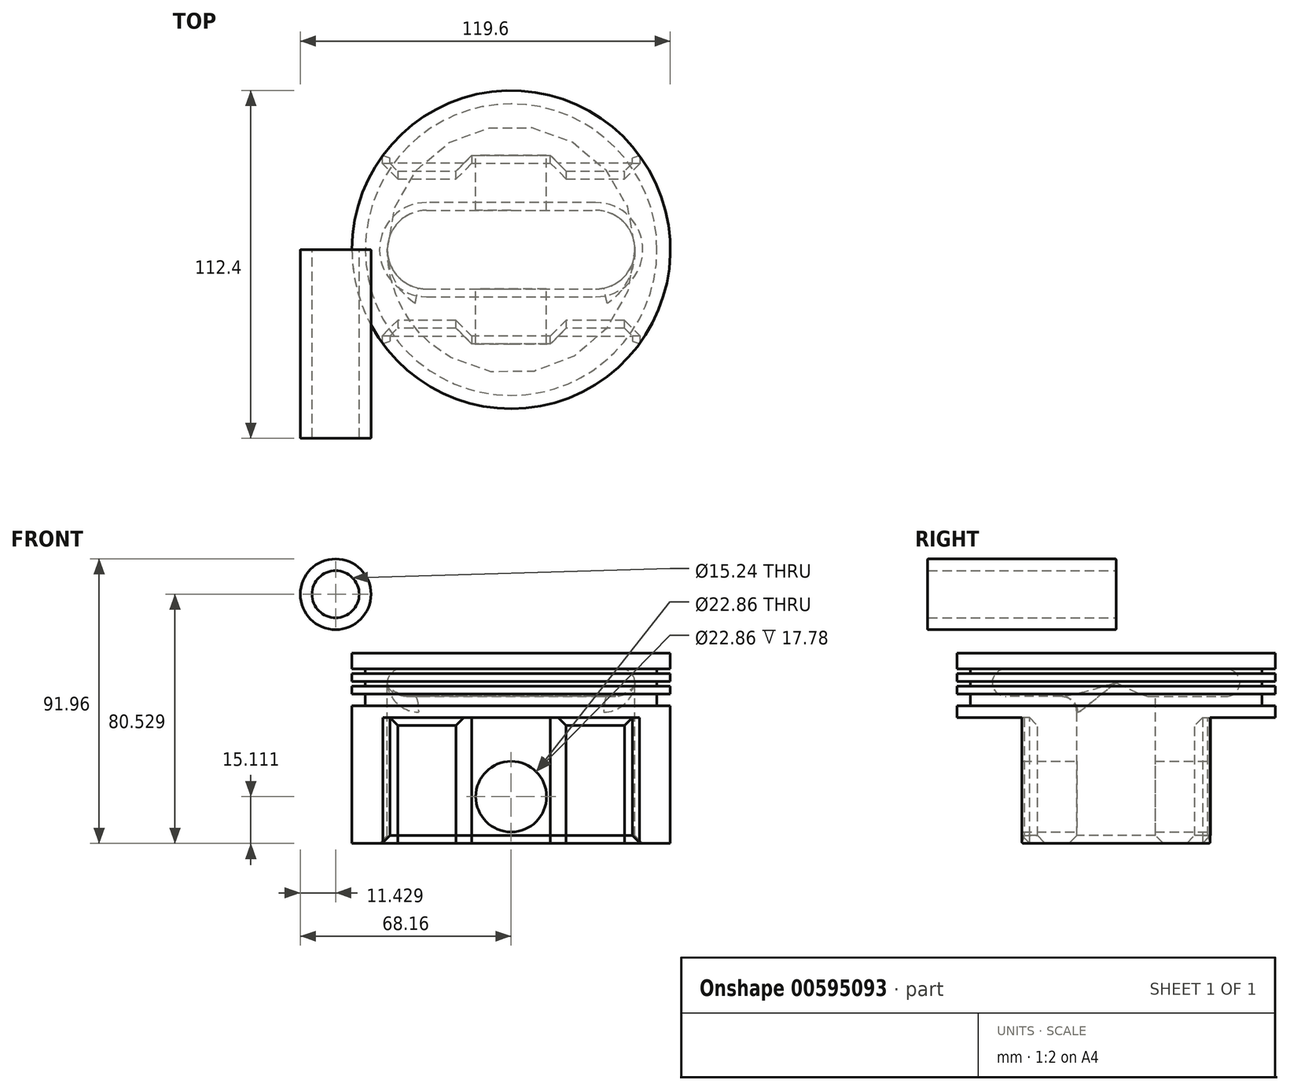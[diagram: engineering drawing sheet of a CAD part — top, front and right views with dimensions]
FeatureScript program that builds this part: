
annotation { "Feature Type Name" : "Feature", "Feature Type Description" : "" }
export const myFeature = defineFeature(function(context is Context, id is Id, definition is map)
    precondition{}
    {
        {
            var Q0;
            Q0=qCreatedBy(makeId("Front.planeOp"),FACE);
            var sketch = newSketch(context, id + "F0", { "sketchPlane" : qUnion([Q0])});
            skLineSegment(sketch, "E0", {"start": v(0, 41.43) * mm, "end": v(-51.44, 41.43) * mm});
            skLineSegment(sketch, "E1", {"start": v(-51.43, 41.43) * mm, "end": v(-51.43, 36.35) * mm});
            skLineSegment(sketch, "E2", {"start": v(-51.44, 36.35) * mm, "end": v(-47.12, 36.35) * mm});
            skLineSegment(sketch, "E3", {"start": v(-47.12, 36.35) * mm, "end": v(-47.12, 34.82) * mm});
            skLineSegment(sketch, "E4", {"start": v(-47.12, 34.82) * mm, "end": v(-51.44, 34.82) * mm});
            skLineSegment(sketch, "E5", {"start": v(-51.43, 34.82) * mm, "end": v(-51.43, 32.28) * mm});
            skLineSegment(sketch, "E6", {"start": v(-51.44, 32.28) * mm, "end": v(-47.12, 32.28) * mm});
            skLineSegment(sketch, "E7", {"start": v(-47.12, 32.28) * mm, "end": v(-47.12, 30.76) * mm});
            skLineSegment(sketch, "E8", {"start": v(-47.12, 30.76) * mm, "end": v(-51.44, 30.76) * mm});
            skLineSegment(sketch, "E9", {"start": v(-51.44, 30.76) * mm, "end": v(-51.44, 28.22) * mm});
            skLineSegment(sketch, "E10", {"start": v(-51.44, 28.22) * mm, "end": v(-47.12, 28.22) * mm});
            skLineSegment(sketch, "E11", {"start": v(-47.12, 28.22) * mm, "end": v(-47.12, 24.4) * mm});
            skLineSegment(sketch, "E12", {"start": v(-47.12, 24.4) * mm, "end": v(-51.44, 24.4) * mm});
            skLineSegment(sketch, "E13", {"start": v(-51.44, 24.4) * mm, "end": v(-51.44, 20.6) * mm});
            skLineSegment(sketch, "E14", {"start": v(-51.44, 20.6) * mm, "end": v(-40, 20.6) * mm});
            skLineSegment(sketch, "E15", {"start": v(0, 20.6) * mm, "end": v(0, 27.46) * mm});
            skLineSegment(sketch, "E16", {"start": v(0, 36.35) * mm, "end": v(-35.56, 36.35) * mm});
            skPoint(sketch, "E17.orphan", {"position": v(-35.56, 27.46) * mm});
            skArc(sketch, "E18", {"start": v(-35.56, 36.35) * mm, "mid": v(-40, 31.9) * mm, "end": v(-35.56, 27.46) * mm});
            skLineSegment(sketch, "E19", {"start": v(-35.56, 27.46) * mm, "end": v(0, 27.46) * mm});
            skLineSegment(sketch, "E20", {"start": v(-40, 20.6) * mm, "end": v(0, 20.6) * mm});
            skLineSegment(sketch, "E21.trimOffspring", {"start": v(0, 36.35) * mm, "end": v(0, 41.43) * mm});
            skSolve(sketch);
        }
        {
            var Q0;
            {var subQ0=sQuery(id+"F0.wireOp",EDGE,"E0");Q0=makeQuery(id+"F0.imprint","IMPRINT",FACE,{"disambiguationData":[TD([[makeQuery(id+"F0.imprint","IMPRINT",EDGE,{"derivedFrom":subQ0}),1.0]])]});}
            var Q1;
            Q1=sQuery(id+"F0.wireOp",EDGE,"E15");
            revolve(context, id + "F1", {"entities" : qUnion([Q0]), "axis" : qUnion([Q1]), "revolveType" : RevolveType.FULL});
        }
        {
            var Q0;
            Q0=makeQuery(id+"F1.opRevolve","SWEPT_FACE",FACE,{"disambiguationData":[OSD([sQuery(id+"F0.wireOp",EDGE,"E14")])]});
            var sketch = newSketch(context, id + "F2", { "sketchPlane" : qUnion([Q0])});
            skLineSegment(sketch, "E22", {"start": v(-39.2, 25.4) * mm, "end": v(-15.24, 25.4) * mm});
            skLineSegment(sketch, "E23", {"start": v(-13.04, 12.7) * mm, "end": v(16, 12.7) * mm, "construction": true});
            skLineSegment(sketch, "E24", {"start": v(-39.2, 25.4) * mm, "end": v(-39.2, 33.3) * mm});
            skLineSegment(sketch, "E25.MirrorCS", {"start": v(39.2, 25.4) * mm, "end": v(39.2, 33.3) * mm});
            skLineSegment(sketch, "E26.MirrorCS", {"start": v(-39.2, -25.4) * mm, "end": v(-15.24, -25.4) * mm});
            skLineSegment(sketch, "E27.MirrorCS", {"start": v(-39.2, -25.4) * mm, "end": v(-39.2, -33.3) * mm});
            skLineSegment(sketch, "E28", {"start": v(0, 12.7) * mm, "end": v(27.3, 12.7) * mm});
            skPoint(sketch, "E28.startSnap0", {"position": v(1.48, 12.7) * mm});
            skLineSegment(sketch, "E29.MirrorCS", {"start": v(0, -12.7) * mm, "end": v(27.3, -12.7) * mm});
            skArc(sketch, "E30", {"start": v(27.3, 12.7) * mm, "mid": v(40, 0) * mm, "end": v(27.3, -12.7) * mm});
            skArc(sketch, "E31.MirrorCS", {"start": v(-27.3, 12.7) * mm, "mid": v(-40, 0) * mm, "end": v(-27.3, -12.7) * mm});
            skLineSegment(sketch, "E32.MirrorCS", {"start": v(0, 12.7) * mm, "end": v(-27.3, 12.7) * mm});
            skLineSegment(sketch, "E33.MirrorCS", {"start": v(0, -12.7) * mm, "end": v(-27.3, -12.7) * mm});
            skLineSegment(sketch, "E34", {"start": v(-15.24, 25.4) * mm, "end": v(-15.24, 30.48) * mm});
            skLineSegment(sketch, "E35", {"start": v(-15.24, 30.48) * mm, "end": v(0, 30.48) * mm});
            skLineSegment(sketch, "E36.MirrorCS", {"start": v(15.24, 30.48) * mm, "end": v(0, 30.48) * mm});
            skLineSegment(sketch, "E37.MirrorCS", {"start": v(15.24, 25.4) * mm, "end": v(15.24, 30.48) * mm});
            skLineSegment(sketch, "E38.MirrorCS", {"start": v(-15.24, -30.48) * mm, "end": v(0, -30.48) * mm});
            skLineSegment(sketch, "E39.MirrorCS", {"start": v(15.24, -30.48) * mm, "end": v(0, -30.48) * mm});
            skLineSegment(sketch, "E40.MirrorCS", {"start": v(15.24, -25.4) * mm, "end": v(15.24, -30.48) * mm});
            skLineSegment(sketch, "E41.MirrorCS", {"start": v(-15.24, -25.4) * mm, "end": v(-15.24, -30.48) * mm});
            skLineSegment(sketch, "E42.trimOffspring", {"start": v(15.24, -25.4) * mm, "end": v(39.2, -25.4) * mm});
            skLineSegment(sketch, "E43.trimOffspring", {"start": v(15.24, 25.4) * mm, "end": v(39.2, 25.4) * mm});
            skPoint(sketch, "E44.orphan", {"position": v(44.73, 25.4) * mm});
            skLineSegment(sketch, "E45.MirrorCS", {"start": v(39.2, -25.4) * mm, "end": v(39.2, -33.3) * mm});
            skPoint(sketch, "E46.orphan", {"position": v(44.73, -25.4) * mm});
            skSolve(sketch);
        }
        {
            var Q0;
            Q0=makeQuery(id+"F2.imprint","IMPRINT",FACE,{"disambiguationData":[TD([[makeQuery(id+"F2.imprint","IMPRINT",EDGE,{"derivedFrom":sQuery(id+"F2.wireOp",EDGE,"E22")}),-1.0]])]});
            extrude(context, id + "F3", {"entities" : qUnion([Q0]), "operationType" : NewBodyOperationType.ADD, "depth" : 40.64 * mm, "offsetDistance" : 25.4 * mm});
        }
        {
            var Q0;
            Q0=makeQuery(id+"F3.opExtrude","SWEPT_FACE",FACE,{"disambiguationData":[OSD([sQuery(id+"F2.wireOp",EDGE,"E38.MirrorCS"),sQuery(id+"F2.wireOp",EDGE,"E39.MirrorCS")])]});
            var sketch = newSketch(context, id + "F4", { "sketchPlane" : qUnion([Q0])});
            skCircle(sketch, "E47", {"center": v(0, -4.93) * mm, "radius": 11.43 * mm});
            skPoint(sketch, "E47.centerSnap0", {"position": v(-15.24, 0.28) * mm});
            skSolve(sketch);
        }
        {
            var Q0;
            Q0=makeQuery(id+"F4.imprint","IMPRINT",FACE,{"disambiguationData":[TD([[makeQuery(id+"F4.imprint","IMPRINT",EDGE,{"derivedFrom":sQuery(id+"F4.wireOp",EDGE,"E47")}),1.0]])]});
            extrude(context, id + "F5", {"entities" : qUnion([Q0]), "operationType" : NewBodyOperationType.REMOVE, "oppositeDirection" : true, "depth" : 77.72 * mm, "offsetDistance" : 25.4 * mm});
        }
        {
            var Q0;
            Q0=makeQuery(id+"F3.opExtrude","SWEPT_EDGE",EDGE,{"disambiguationData":[OSD([sQuery(id+"F2.wireOp",EDGE,"E38.MirrorCS"),sQuery(id+"F2.wireOp",EDGE,"E41.MirrorCS")])]});
            var Q1;
            Q1=makeQuery(id+"F3.opExtrude","SWEPT_EDGE",EDGE,{"disambiguationData":[OSD([sQuery(id+"F2.wireOp",EDGE,"E26.MirrorCS"),sQuery(id+"F2.wireOp",EDGE,"E41.MirrorCS")])]});
            var Q2;
            Q2=makeQuery(id+"F3.opExtrude","CAP_EDGE",EDGE,{"disambiguationData":[OSD([sQuery(id+"F2.wireOp",EDGE,"E26.MirrorCS")])],"isStart":false});
            var Q3;
            Q3=makeQuery(id+"F3.opExtrude","CAP_EDGE",EDGE,{"disambiguationData":[OSD([sQuery(id+"F2.wireOp",EDGE,"E27.MirrorCS")])],"isStart":false});
            var Q4;
            Q4=makeQuery(id+"F3.opExtrude","CAP_EDGE",EDGE,{"disambiguationData":[OSD([sQuery(id+"F2.wireOp",EDGE,"E42.trimOffspring")])],"isStart":false});
            var Q5;
            Q5=makeQuery(id+"F3.opExtrude","SWEPT_FACE",FACE,{"disambiguationData":[OSD([sQuery(id+"F2.wireOp",EDGE,"E26.MirrorCS")])]});
            var Q6;
            Q6=makeQuery(id+"F3.opExtrude","SWEPT_FACE",FACE,{"disambiguationData":[OSD([sQuery(id+"F2.wireOp",EDGE,"E42.trimOffspring")])]});
            var Q7;
            Q7=makeQuery(id+"F3.opExtrude","SWEPT_EDGE",EDGE,{"disambiguationData":[OSD([sQuery(id+"F2.wireOp",EDGE,"E39.MirrorCS"),sQuery(id+"F2.wireOp",EDGE,"E40.MirrorCS")])]});
            var Q8;
            Q8=makeQuery(id+"F3.opExtrude","CAP_EDGE",EDGE,{"disambiguationData":[OSD([sQuery(id+"F2.wireOp",EDGE,"E38.MirrorCS"),sQuery(id+"F2.wireOp",EDGE,"E39.MirrorCS")])],"isStart":false});
            var Q9;
            Q9=makeQuery(id+"F3.opExtrude","SWEPT_FACE",FACE,{"disambiguationData":[OSD([sQuery(id+"F2.wireOp",EDGE,"E43.trimOffspring")])]});
            var Q10;
            Q10=makeQuery(id+"F3.opExtrude","SWEPT_FACE",FACE,{"disambiguationData":[OSD([sQuery(id+"F2.wireOp",EDGE,"E22")])]});
            var Q11;
            Q11=makeQuery(id+"F3.opExtrude","CAP_EDGE",EDGE,{"disambiguationData":[OSD([sQuery(id+"F2.wireOp",EDGE,"E35"),sQuery(id+"F2.wireOp",EDGE,"E36.MirrorCS")])],"isStart":false});
            var Q12;
            Q12=makeQuery(id+"F3.opExtrude","SWEPT_EDGE",EDGE,{"disambiguationData":[OSD([sQuery(id+"F2.wireOp",EDGE,"E36.MirrorCS"),sQuery(id+"F2.wireOp",EDGE,"E37.MirrorCS")])]});
            var Q13;
            Q13=makeQuery(id+"F3.opExtrude","SWEPT_EDGE",EDGE,{"disambiguationData":[OSD([sQuery(id+"F2.wireOp",EDGE,"E34"),sQuery(id+"F2.wireOp",EDGE,"E35")])]});
            chamfer(context, id + "F6", {"entities" : qUnion([Q0, Q1, Q2, Q3, Q4, Q5, Q6, Q7, Q8, Q9, Q10, Q11, Q12, Q13]), "width" : 2.54 * mm, "tangentPropagation" : true});
        }
        {
            var Q0;
            Q0=makeQuery(id+"F3.opExtrude","SWEPT_EDGE",EDGE,{"disambiguationData":[OSD([sQuery(id+"F0.wireOp",EDGE,"E13"),sQuery(id+"F0.wireOp",EDGE,"E14"),sQuery(id+"F2.wireOp",EDGE,"E45.MirrorCS")])]});
            var Q1;
            Q1=makeQuery(id+"F3.opExtrude","SWEPT_EDGE",EDGE,{"disambiguationData":[OSD([sQuery(id+"F0.wireOp",EDGE,"E13"),sQuery(id+"F0.wireOp",EDGE,"E14"),sQuery(id+"F2.wireOp",EDGE,"E27.MirrorCS")])]});
            var Q2;
            Q2=makeQuery(id+"F3.opExtrude","SWEPT_EDGE",EDGE,{"disambiguationData":[OSD([sQuery(id+"F0.wireOp",EDGE,"E13"),sQuery(id+"F0.wireOp",EDGE,"E14"),sQuery(id+"F2.wireOp",EDGE,"E24")])]});
            var Q3;
            Q3=makeQuery(id+"F3.opExtrude","SWEPT_EDGE",EDGE,{"disambiguationData":[OSD([sQuery(id+"F0.wireOp",EDGE,"E13"),sQuery(id+"F0.wireOp",EDGE,"E14"),sQuery(id+"F2.wireOp",EDGE,"E25.MirrorCS")])]});
            chamfer(context, id + "F7", {"entities" : qUnion([Q0, Q1, Q2, Q3]), "width" : 1.27 * mm, "tangentPropagation" : true});
        }
        {
            var Q0;
            Q0=makeQuery(id+"F3.opExtrude","CAP_EDGE",EDGE,{"disambiguationData":[OSD([sQuery(id+"F2.wireOp",EDGE,"E30")])],"isStart":false});
            chamfer(context, id + "F8", {"entities" : qUnion([Q0]), "width" : 2.54 * mm, "tangentPropagation" : true});
        }
        {
            var Q0;
            Q0=makeQuery(id+"F3.boolean.opBoolean","SPLIT",FACE,{"disambiguationData":[TD([makeQuery(id+"F3.opExtrude","SWEPT_FACE",FACE,{"disambiguationData":[OSD([sQuery(id+"F2.wireOp",EDGE,"E30")])]})])],"derivedFrom":makeQuery(id+"F1.opRevolve","SWEPT_FACE",FACE,{"disambiguationData":[OSD([sQuery(id+"F0.wireOp",EDGE,"E14"),sQuery(id+"F0.wireOp",EDGE,"E20")])]})});
            extrude(context, id + "F9", {"entities" : qUnion([Q0]), "operationType" : NewBodyOperationType.REMOVE, "oppositeDirection" : true, "depth" : 11.18 * mm, "offsetDistance" : 25.4 * mm});
        }
        {
            var Q0;
            Q0=makeQuery(id+"F9.boolean.opBoolean","INTERSECT",EDGE,{"derivedFrom":[makeQuery(id+"F1.opRevolve","SWEPT_FACE",FACE,{"disambiguationData":[OSD([sQuery(id+"F0.wireOp",EDGE,"E19")])]}),makeQuery(id+"F9.opExtrude","SWEPT_FACE",FACE,{"disambiguationData":[OSD([sQuery(id+"F2.wireOp",EDGE,"E28"),sQuery(id+"F2.wireOp",EDGE,"E32.MirrorCS")])]})]});
            fillet(context, id + "F10", {"entities" : qUnion([Q0]), "radius" : 5.08 * mm, "tangentPropagation" : true, "allowEdgeOverflow" : false});
        }
        {
            var Q0;
            Q0=qCreatedBy(makeId("Front.planeOp"),FACE);
            var sketch = newSketch(context, id + "F11", { "sketchPlane" : qUnion([Q0])});
            skCircle(sketch, "E48", {"center": v(-56.73, 60.49) * mm, "radius": 11.43 * mm});
            skCircle(sketch, "E49.0", {"center": v(-56.73, 60.49) * mm, "radius": 7.62 * mm});
            skSolve(sketch);
        }
        {
            var Q0;
            Q0=makeQuery(id+"F11.imprint","IMPRINT",FACE,{"disambiguationData":[TD([[makeQuery(id+"F11.imprint","IMPRINT",EDGE,{"derivedFrom":sQuery(id+"F11.wireOp",EDGE,"E48")}),1.0]])]});
            extrude(context, id + "F12", {"entities" : qUnion([Q0]), "depth" : 60.96 * mm, "offsetDistance" : 25.4 * mm});
        }
        {
            var Q0;
            Q0=makeQuery(id+"F12.opExtrude","CAP_FACE",FACE,{"disambiguationData":[OSD([sQuery(id+"F11.wireOp",EDGE,"E48"),sQuery(id+"F11.wireOp",EDGE,"E49.0")])],"isStart":false});
            var Q1;
            Q1=makeQuery(id+"F12.opExtrude","CAP_FACE",FACE,{"disambiguationData":[OSD([sQuery(id+"F11.wireOp",EDGE,"E48"),sQuery(id+"F11.wireOp",EDGE,"E49.0")])],"isStart":true});
            var Q2;
            Q2=makeQuery(id+"F5.boolean.opBoolean","COPY",EDGE,{"derivedFrom":makeQuery(id+"F5.opExtrude","CAP_EDGE",EDGE,{"disambiguationData":[OSD([sQuery(id+"F4.wireOp",EDGE,"E47")])],"isStart":true})});
            var Q3;
            Q3=makeQuery(id+"F5.boolean.opBoolean","INTERSECT",EDGE,{"derivedFrom":[makeQuery(id+"F3.opExtrude","SWEPT_FACE",FACE,{"disambiguationData":[OSD([sQuery(id+"F2.wireOp",EDGE,"E35"),sQuery(id+"F2.wireOp",EDGE,"E36.MirrorCS")])]}),makeQuery(id+"F5.opExtrude","SWEPT_FACE",FACE,{"disambiguationData":[OSD([sQuery(id+"F4.wireOp",EDGE,"E47")])]})]});
            fillet(context, id + "F13", {"entities" : qUnion([Q0, Q1, Q2, Q3]), "radius" : 0.25 * mm, "tangentPropagation" : true, "allowEdgeOverflow" : false});
        }
    });
